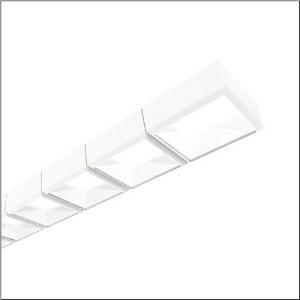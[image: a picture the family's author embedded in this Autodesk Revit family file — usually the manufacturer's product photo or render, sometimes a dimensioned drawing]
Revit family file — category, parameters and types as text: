
# Revit family: scriptus_r__11_5mz313d0twb_9c96
name_source: partatom
category: Lighting Fixtures
units: mm (PartAtom-declared; Revit-internal decimal feet)

## family parameters
Cut with Voids When Loaded = No
Host = Face
Light Source = No
Part Type = Normal
Room Calculation Point = No
Round Connector Dimension = Use Diameter
Shared = No

## types (1)
- --- (1 x LED 3000K+6500K / CRI = 80 (unbekannt), 3390 lm / 3550 lm, 3000K)
    Apparent Load = 107 VA
    CIE Flux Codes = 0 0 0 0 100 / 82 95 99 100 100
    Color Rendering = 80
    Color Temperature = 3000K
    Default Elevation = 1800 mm
    Description = Scriptus® 11, office luminaire, primary optical cover: lenses, CAT 2 (L<= 3000cd/m²), light emission: direct/indirect distribution, primary light characteristic: symmetric, installation type: suspended mounting, LED, rated luminous flux: 13.880lm, luminous efficacy: 126lm/W, light colour: 8tw, colour temperature: 3000..6500K, control gear: DALI DT8, with terminal, 5-pole, mains connection: 230V, AC, 50Hz, rated input power: 110W, LED, control gear: ECG DALI, housing, luminaire housing, of aluminium, traffic white (RAL 9016), length: 2.648mm, width: 114mm, height: 57mm, protection rating (complete): IP20, insulation class (complete): insulation class I (protective earthing), certification: CE, protection symbol: F, permissible operating ambient temperature: <= +25°C, standard: EN 50419, packaging unit: 1 piece
    Height = 57 mm
    Lamp = 1 x LED 3000K+6500K / CRI >= 80 (unbekannt)
    Lamp Light Flux = 3390 lm / 3550 lm
    Lamp count = 1
    Length = 2648 mm
    Luminous efficacy = 130 lm/W
    Manufacturer = Siteco
    ModVariant = No
    Model = 5MZ313D0TWB
    Mounting Place = Ceiling
    Mounting Type = Pendant
    Number of Poles = 1
    OnlyDefault = Yes
    Power Factor = 1
    Product Name = Scriptus® 11
    Product group = office luminaire | ceiling pendant
    ProductGroupID = 904
    Protection Class = Protection class I
    Protection Degree = IP 20
    RLX_Detail_Level = 1
    RLX_Emergency_Light_Flux = 0 lm
    RLX_Emergency_Type = 0
    RLX_Emergency_Type_DB = No
    RlxData = <blob elided: 31993 chars, md5=047d5aa6>
    Socket = socket
    Standby Power = 0 W
    System Light Flux = 13880 lm
    System Power = 107 W
    Type Comments = individual setting: colour temperature 6500K
    Type Image = l_1004839.jpg
    URL = http://relux.com
    VarID = @adj_203049
    Voltage = 0 V
    Weight = 0.00 kg
    Width = 114 mm

## geometry (parser evidence)
native form markers: Blend x4, Sweep x17
no freeform markers — native parametric forms only
